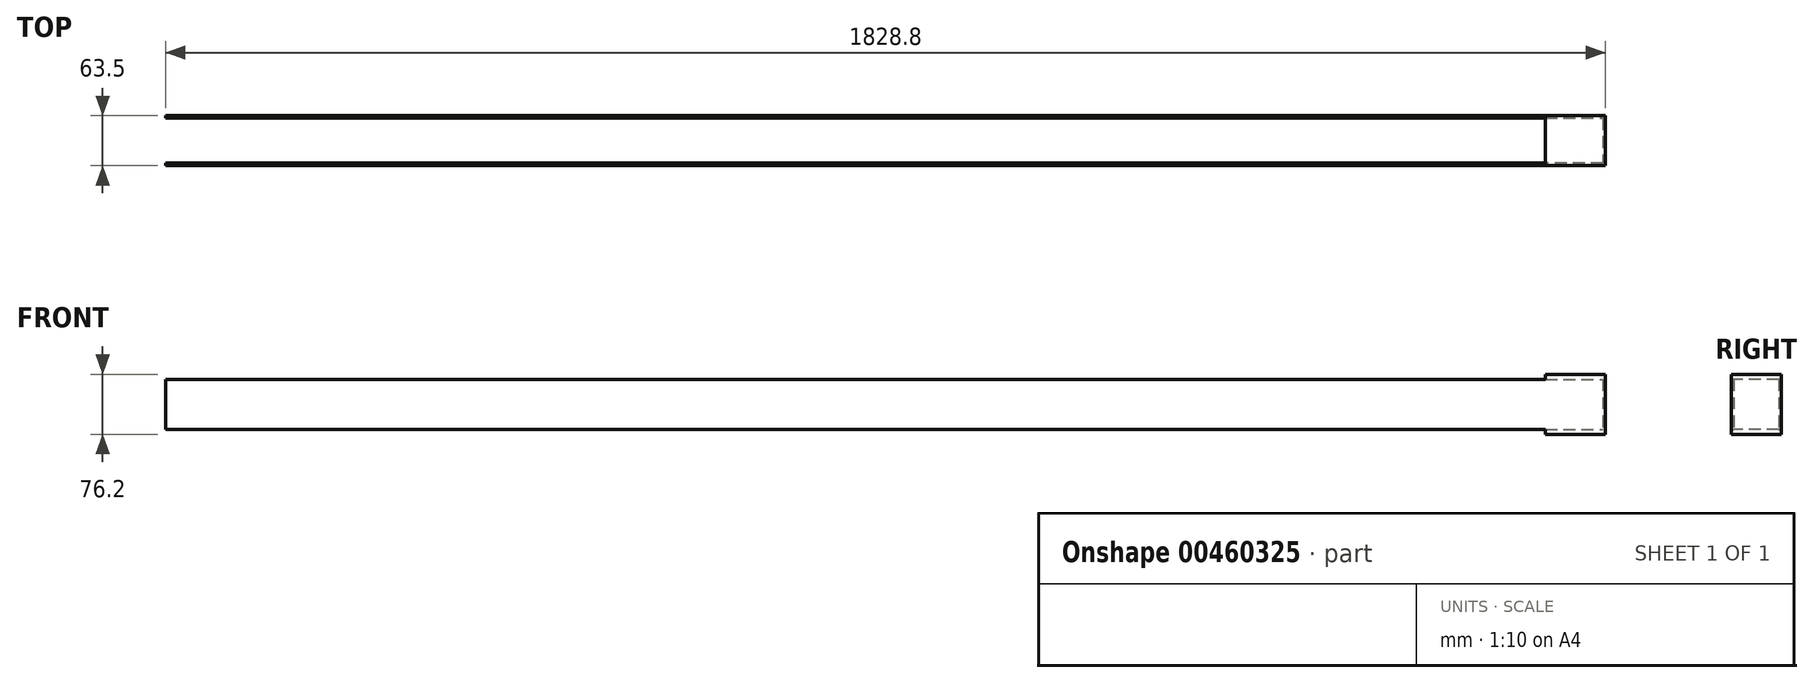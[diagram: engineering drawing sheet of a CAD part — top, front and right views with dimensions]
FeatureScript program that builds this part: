
annotation { "Feature Type Name" : "Feature", "Feature Type Description" : "" }
export const myFeature = defineFeature(function(context is Context, id is Id, definition is map)
    precondition{}
    {
        {
            var Q0;
            Q0=qCreatedBy(makeId("Top.planeOp"),FACE);
            var sketch = newSketch(context, id + "F0", { "sketchPlane" : qUnion([Q0])});
            skLineSegment(sketch, "E0", {"start": v(0, 31.75) * mm, "end": v(1828.8, 31.75) * mm});
            skLineSegment(sketch, "E1", {"start": v(1828.8, 31.75) * mm, "end": v(1828.8, -31.75) * mm});
            skLineSegment(sketch, "E2", {"start": v(1828.8, -31.75) * mm, "end": v(0, -31.75) * mm});
            skLineSegment(sketch, "E3", {"start": v(0, 31.75) * mm, "end": v(0, -31.75) * mm, "construction": true});
            skLineSegment(sketch, "E4.0", {"start": v(1825.63, -28.57) * mm, "end": v(0, -28.58) * mm});
            skLineSegment(sketch, "E4.1", {"start": v(1825.63, 28.57) * mm, "end": v(1825.63, -28.57) * mm});
            skLineSegment(sketch, "E4.2", {"start": v(0, 28.57) * mm, "end": v(1825.63, 28.58) * mm});
            skLineSegment(sketch, "E5", {"start": v(0, 31.75) * mm, "end": v(0, 28.57) * mm});
            skLineSegment(sketch, "E6", {"start": v(0, -28.58) * mm, "end": v(0, -31.75) * mm});
            skSolve(sketch);
        }
        {
            var Q0;
            Q0 = qSketchRegion(id + "F0", true);
            extrude(context, id + "F1", {"entities" : qUnion([Q0]), "endBound" : BoundingType.SYMMETRIC, "depth" : 63.5 * mm});
        }
        {
            var Q0;
            Q0=makeQuery(id+"F1.opExtrude","CAP_FACE",FACE,{"disambiguationData":[OSD([sQuery(id+"F0.wireOp",EDGE,"E0"),sQuery(id+"F0.wireOp",EDGE,"E1"),sQuery(id+"F0.wireOp",EDGE,"E2"),sQuery(id+"F0.wireOp",EDGE,"E4.0"),sQuery(id+"F0.wireOp",EDGE,"E4.1"),sQuery(id+"F0.wireOp",EDGE,"E4.2"),sQuery(id+"F0.wireOp",EDGE,"E5"),sQuery(id+"F0.wireOp",EDGE,"E6")])],"isStart":false});
            var sketch = newSketch(context, id + "F2", { "sketchPlane" : qUnion([Q0])});
            skLineSegment(sketch, "E7.bottom", {"start": v(1828.8, 31.75) * mm, "end": v(1752.6, 31.75) * mm});
            skLineSegment(sketch, "E7.top", {"start": v(1828.8, -31.75) * mm, "end": v(1752.6, -31.75) * mm});
            skLineSegment(sketch, "E7.left", {"start": v(1828.8, 31.75) * mm, "end": v(1828.8, -31.75) * mm});
            skLineSegment(sketch, "E7.right", {"start": v(1752.6, 31.75) * mm, "end": v(1752.6, -31.75) * mm});
            skSolve(sketch);
        }
        {
            var Q0;
            Q0 = qSketchRegion(id + "F2", true);
            extrude(context, id + "F3", {"entities" : qUnion([Q0]), "operationType" : NewBodyOperationType.ADD, "depth" : 6.35 * mm});
        }
        {
            var Q0;
            Q0=makeQuery(id+"F1.opExtrude","CAP_FACE",FACE,{"disambiguationData":[OSD([sQuery(id+"F0.wireOp",EDGE,"E0"),sQuery(id+"F0.wireOp",EDGE,"E1"),sQuery(id+"F0.wireOp",EDGE,"E2"),sQuery(id+"F0.wireOp",EDGE,"E4.0"),sQuery(id+"F0.wireOp",EDGE,"E4.1"),sQuery(id+"F0.wireOp",EDGE,"E4.2"),sQuery(id+"F0.wireOp",EDGE,"E5"),sQuery(id+"F0.wireOp",EDGE,"E6")])],"isStart":true});
            var sketch = newSketch(context, id + "F4", { "sketchPlane" : qUnion([Q0])});
            skLineSegment(sketch, "E8.bottom", {"start": v(1828.8, 31.75) * mm, "end": v(1752.6, 31.75) * mm});
            skLineSegment(sketch, "E8.top", {"start": v(1828.8, -31.75) * mm, "end": v(1752.6, -31.75) * mm});
            skLineSegment(sketch, "E8.left", {"start": v(1828.8, 31.75) * mm, "end": v(1828.8, -31.75) * mm});
            skLineSegment(sketch, "E8.right", {"start": v(1752.6, 31.75) * mm, "end": v(1752.6, -31.75) * mm});
            skSolve(sketch);
        }
        {
            var Q0;
            Q0 = qSketchRegion(id + "F4", true);
            extrude(context, id + "F5", {"entities" : qUnion([Q0]), "operationType" : NewBodyOperationType.ADD, "depth" : 6.35 * mm});
        }
    });
